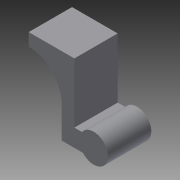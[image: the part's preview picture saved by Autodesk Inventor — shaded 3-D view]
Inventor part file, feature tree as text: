
AUTODESK INVENTOR PART (.ipt)
format: ipt  version: 2015 (Build 190159000, 159)  size: 177,152 bytes
history: native  units: in
note: dims shown in document units (in); Inventor stores cm internally (conversion verified against a paired STEP export)
features: extrude x10, sketch x10, mirror x3, reference x2, projected_geometry x2, fillet x1
ambient origin geometry x8: Origin, YZ Plane, XZ Plane, XY Plane, X Axis, Y Axis, Z Axis, Center Point
bodies: Solid1 (feature_tree)
feature tree (28):
  extrude  "Extrusion1"  Depth=0.9375in TaperAngle=0.0deg
  extrude  "Extrusion2"  Depth=0.4882in TaperAngle=0.0deg
  mirror  "Mirror1"
  extrude  "Extrusion3"  Depth=0.4331in TaperAngle=0.0deg
  extrude  "Extrusion4"  Depth=0.3831in
  mirror  "Mirror2"
  extrude  "Extrusion5"  Depth=1.0in
  fillet  "Fillet3"  Radius=1.0in
  extrude  "Extrusion6"  Depth=1.0in
  mirror  "Mirror4"
  extrude  "Extrusion7"  Depth=0.431in
  extrude  "Extrusion8"  Depth=0.216in TaperAngle=0.0deg
  extrude  "Extrusion9"  [1 undecoded]
  extrude  "Extrusion10"  [1 undecoded]
  sketch  "Sketch1"  dims[d0=0.375in d1=0.0in d2=0.9375in d3=0.0in]
  reference  "Reference1"
  sketch  "Sketch2"  dims[d4=0.3125in d5=0.4882in d6=0.0in]
  sketch  "Sketch3"  dims[d7=0.4331in d8=0.0591in d9=0.0in]
  sketch  "Sketch4"  dims[d11=2.3455in d12=0.3831in]
  sketch  "Sketch7"  dims[d13=1.0in d14=0.0in d16=1.0in d17=1.0in d18=0.0in]
  projected_geometry  "Projected Loop1"
  sketch  "Sketch9"  dims[d19=1.0in d20=0.0in d21=0.25in]
  projected_geometry  "Projected Loop2"
  sketch  "Sketch10"  dims[d22=1.0in d23=0.0in d24=0.431in]
  reference  "Reference2"
  sketch  "Sketch11"  dims[d25=0.216in d26=0.0in d27=0.216in d28=0.0in]
  sketch  "Sketch12"
  sketch  "Sketch13"
note: 2 required parameter values undecoded (feature->parameter linkage not recoverable at this tier; creation-order binding heuristic only, values carry confidence <= 0.55)
